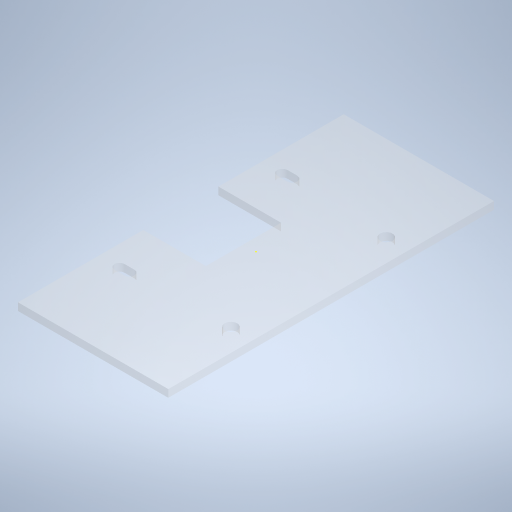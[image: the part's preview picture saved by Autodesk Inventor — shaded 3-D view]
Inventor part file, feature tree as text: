
AUTODESK INVENTOR PART (.ipt)
format: ipt  version: 2024 (Build 280153000, 153)  size: 289,280 bytes
history: native  units: mm
features: sketch x3, extrude x2, other x1
ambient origin geometry x8: Origin, YZ Plane, XZ Plane, XY Plane, X Axis, Y Axis, Z Axis, Center Point
bodies: Body1 (feature_tree)
feature tree (6):
  other  "솔리드1"
  extrude  "돌출1"  Depth=130.0mm
  sketch  "스케치2"
  extrude  "돌출2"  Depth=60.0mm
  sketch  "스케치1"
  sketch  "스케치3"
